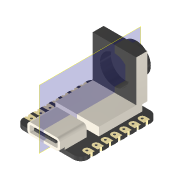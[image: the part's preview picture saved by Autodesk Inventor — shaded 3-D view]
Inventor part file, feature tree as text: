
AUTODESK INVENTOR PART (.ipt)
format: ipt  version: 2022 (Build 260153000, 153)  size: 306,176 bytes
history: native  units: mm
features: extrude x2, sketch x2, projected_geometry x2, plane x1
ambient origin geometry x8: Origin, YZ Plane, XZ Plane, XY Plane, X Axis, Y Axis, Z Axis, Center Point
bodies: Volumenkörper1 (feature_tree), Body1 (feature_tree)
feature tree (7):
  extrude  "Extrusion1"  Depth=3.0mm TaperAngle=0.0deg
  extrude  "Extrusion2"  Depth=12.0mm
  plane  "Arbeitsebene1"
  sketch  "Skizze1"  dims[d0=8.0mm d1=3.0mm d2=0.0mm]
  projected_geometry  "Projizierte Kontur1"
  sketch  "Skizze2"  dims[d3=12.0mm d4=12.0mm d5=3.0mm d6=0.0mm]
  projected_geometry  "Projizierte Kontur2"
